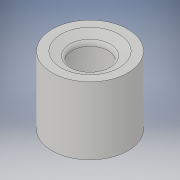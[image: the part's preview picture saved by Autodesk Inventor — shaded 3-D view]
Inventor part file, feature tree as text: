
AUTODESK INVENTOR PART (.ipt)
format: ipt  version: 2017 (Build 210142000, 142)  size: 158,720 bytes
history: native  units: in
note: dims shown in document units (in); Inventor stores cm internally (conversion verified against a paired STEP export)
features: revolve x1, sketch x1
ambient origin geometry x8: Origin, YZ Plane, XZ Plane, XY Plane, X Axis, Y Axis, Z Axis, Center Point
bodies: Solid1 (feature_tree)
feature tree (2):
  revolve  "Revolution1"  [1 undecoded]
  sketch  "Sketch1"  dims[d0=1.13in d1=3.7in d2=0.125in d3=0.1718in d5=1.0in d6=1.0in d7=90.0deg d8=0.5in d9=15.0deg d12=1.25in d13=0.25in d16=0.5in d17=0.5in d18=0.5in d19=2.5in d20=0.5in d22=0.375in d23=0.25in d25=0.234in d26=15.0deg d27=0.125in d28=0.25in d29=1.0in d30=4.25in d31=0.25in d32=1.0in d33=90.0deg]
note: 1 required parameter value undecoded (feature->parameter linkage not recoverable at this tier; creation-order binding heuristic only, values carry confidence <= 0.55)
